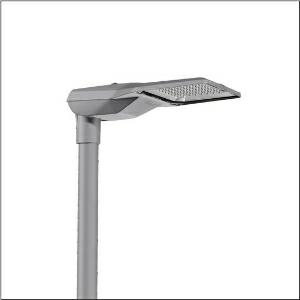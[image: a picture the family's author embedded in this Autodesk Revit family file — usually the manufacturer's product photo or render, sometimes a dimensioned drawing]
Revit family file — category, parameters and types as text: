
# Revit family: streetlight_sl_21_midi___stw1_0a_5xe3e33s08lb_8a64
name_source: partatom
category: Lighting Fixtures
units: mm (PartAtom-declared; Revit-internal decimal feet)

## family parameters
Cut with Voids When Loaded = No
Host = Face
Light Source = No
Part Type = Normal
Room Calculation Point = No
Round Connector Dimension = Use Diameter
Shared = No

## types (1)
- --- (1 x LED, 14340 lm, 99.6 W, 3000K)
    Apparent Load = 100 VA
    CIE Flux Codes = 38 75 98 100 100
    Color Rendering = 70
    Color Temperature = 3000K
    Default Elevation = 1800 mm
    Description = Streetlight SL 21 midi, mast luminaire, primary light control with lens, of PMMA, primary optical cover: cover, of toughened safety glass, transparent, light distribution: STW1.0a, light emission: direct distribution, primary light characteristic: asymmetric, installation type: side-entry, post-top, LED, High Power LED, rated luminous flux: 14.340lm, luminous efficacy: 144lm/W, light colour: 730, colour temperature: 3000K, control gear: D4i, control: overheat protection, constant luminous flux control, time-dependent luminous flux control, flexible luminous flux parameterisation, pre-setting: logarithmic dimming characteristic, mains connection: 230..240V, AC, 50/60Hz, start of lifetime: 100W, end of service life: 102W, reduction: 46W, luminaire housing, of diecast aluminium, powder-coated, Siteco® metallic grey (DB 702S), corrosivity category C5 mid according to DIN EN ISO 12944, please order mast flange separately, inclination adjustable: 0°, 5°, 10°, 15°, sealing non-destructively replaceable, multi-level sealing system, length: 644mm, width: 335mm, height: 110mm, mast flange for spigot size: 42mm (side-entry): 5XC10008XM4, 60/48mm (side-entry/post-top): 5XC10108XM2, 76/60mm (side-entry/post-top): 5XC10108XM1, mounting height: 4..8m, Smart Interface above, protection rating (complete): IP66, insulation class (complete): insulation class II (safety insulation), certification: CE, ENEC, ENEC+, VDE, impact resistance: IK10, permissible operating ambient temperature for outdoor applications: -40..+50°C, standard-compliant lighting for roads and squares, packaging unit: 1 piece

Light Distribution: STW1.0a
    Height = 111 mm
    Lamp = 1 x LED
    Lamp Light Flux = 14340 lm
    Lamp Power = 99.6 W
    Lamp count = 1
    Length = 644 mm
    Luminous efficacy = 144 lm/W
    Manufacturer = Siteco
    ModVariant = No
    Model = 5XE3E33S08LB
    Number of Poles = 1
    OnlyDefault = Yes
    Power Factor = 1
    Product Name = Streetlight SL 21 midi | STW1.0a
    Product group = mast luminaire | pylon top
    ProductGroupID = 6100
    Protection Class = Protection class II
    Protection Degree = IP 66
    RLX_Detail_Level = 1
    RLX_Emergency_Light_Flux = 0 lm
    RLX_Emergency_Type = 0
    RLX_Emergency_Type_DB = No
    RlxData = <blob elided: 26881 chars, md5=b36fe345>
    Socket = socket
    Standby Power = 0 W
    System Light Flux = 14340 lm
    System Power = 100 W
    Type Comments = factory setting: luminous flux: 100 % | dim-lin: 254 | 1020 mA
    Type Image = l_1004302.jpg
    URL = http://relux.com
    VarID = @adj_031705
    Voltage = 0 V
    Weight = 0.00 kg
    Width = 336 mm

## geometry (parser evidence)
native form markers: Blend x4, Sweep x11
no freeform markers — native parametric forms only
